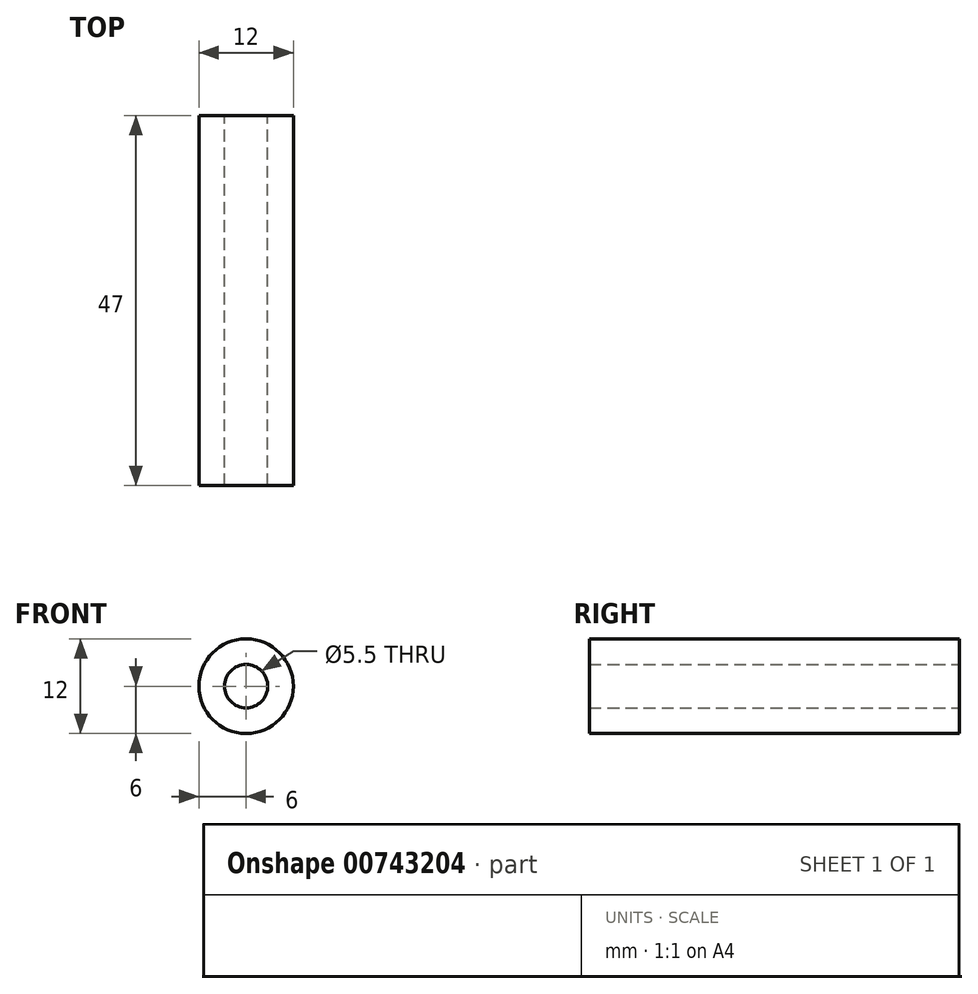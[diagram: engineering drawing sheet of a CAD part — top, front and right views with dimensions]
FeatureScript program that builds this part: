
annotation { "Feature Type Name" : "Feature", "Feature Type Description" : "" }
export const myFeature = defineFeature(function(context is Context, id is Id, definition is map)
    precondition{}
    {
        {
            var Q0;
            Q0=qCreatedBy(makeId("Front.planeOp"),FACE);
            var sketch = newSketch(context, id + "F0", { "sketchPlane" : qUnion([Q0])});
            skCircle(sketch, "E0", {"center": v(0, 0) * mm, "radius": 6 * mm});
            skCircle(sketch, "E1", {"center": v(0, 0) * mm, "radius": 2.75 * mm});
            skSolve(sketch);
        }
        {
            var Q0;
            Q0=makeQuery(id+"F0.imprint","IMPRINT",FACE,{"disambiguationData":[TD([[makeQuery(id+"F0.imprint","IMPRINT",EDGE,{"derivedFrom":sQuery(id+"F0.wireOp",EDGE,"E0")}),1.0]])]});
            extrude(context, id + "F1", {"entities" : qUnion([Q0]), "depth" : 47 * mm, "offsetDistance" : 25 * mm});
        }
    });
